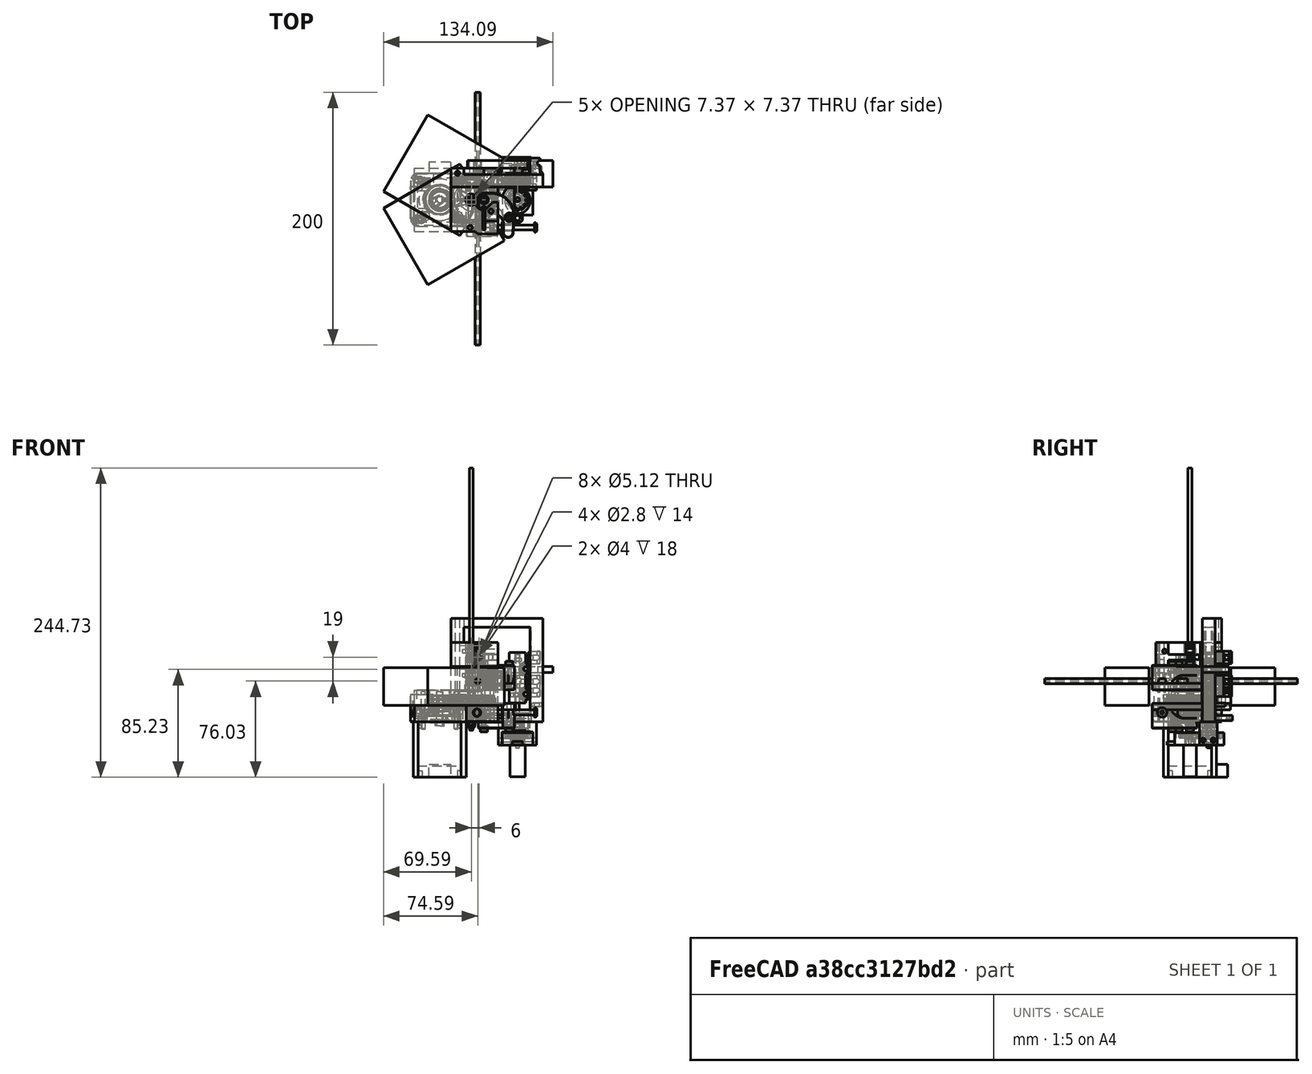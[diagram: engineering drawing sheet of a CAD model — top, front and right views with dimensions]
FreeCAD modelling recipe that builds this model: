
FCSTD DOCUMENT  (FreeCAD 0.17R13541 (Git))
Label: multi-drive
License: All rights reserved
LicenseURL: http://en.wikipedia.org/wiki/All_rights_reserved
objects: Part::Cylinder×120, Part::Feature×74, Part::MultiFuse×72, Part::Box×64, Part::Cut×51, Part::Mirroring×21, Part::Chamfer×13, App::DocumentObjectGroup×8, Part::Fillet×5, Part::MultiCommon×2, Part::Fuse×2
note: 424 computed .brp shape members not serialized (recipe doc carries the construction recipe); baked Part::Feature solids carry a one-line shape summary decoded from their .brp

FEATURE [Part::Feature] Part__Feature  label="408"
  Placement = pos=(-0.0297872,0.0238949,-17.7265) rot=(0,0,-1;1.5708rad)
  shape: bbox 42 x 50.7 x 67.75 mm, 52 faces (baked)
FEATURE [Part::Feature] Part__Feature001  label="279"
  Placement = pos=(33.9857,-1.05205,32.8235) rot=(0.910043,0.414513,0;3.14159rad)
  shape: bbox 10 x 10 x 4 mm, 22 faces (baked)
FEATURE [Part::Feature] Part__Feature002  label="1308_lasercut"
  Placement = pos=(34.9702,0.079623,40.5235) rot=(1,0,0;3.14159rad)
  shape: bbox 28.5 x 62 x 5 mm, 26 faces (baked)
FEATURE [Part::Feature] Part__Feature003  label="1309"
  Placement = pos=(34.9702,0.079623,29.0235) rot=(1,0,0;3.14159rad)
  shape: bbox 39.69 x 36.58 x 16.55 mm, 81 faces (baked)
FEATURE [Part::Feature] Part__Feature004  label="1193"
  Placement = pos=(39.781,-21.9761,33.5235) rot=(0.447214,0.774597,0.447214;1.82348rad)
  shape: bbox 3.2 x 7 x 8.083 mm, 26 faces (baked)
FEATURE [Part::Feature] Part__Feature005  label="650"
  Placement = pos=(74.781,-21.9761,33.5235) rot=(-0.322847,0.889685,-0.322847;1.68742rad)
  shape: bbox 37.2 x 8.193 x 8.193 mm, 18 faces (baked)
FEATURE [Part::Feature] Part__Feature006  label="1185"
  Placement = pos=(49.1702,-21.9761,33.5235) rot=(0.682107,-0.263555,0.682107;3.65698rad)
  shape: bbox 0.8 x 9 x 9 mm, 6 faces (baked)
FEATURE [Part::Feature] Part__Feature007  label="212"
  Placement = pos=(34.9702,0.079623,35.8235) rot=(0.929679,0.36837,0;3.14159rad)
  shape: bbox 7 x 7 x 0.5 mm, 6 faces (baked)
FEATURE [Part::Feature] Part__Feature008  label="257"
  Placement = pos=(34.9702,0.079623,21.0235) rot=(0.969952,-0.243295,0;3.14159rad)
  shape: bbox 5.7 x 5.7 x 15 mm, 16 faces (baked)
FEATURE [Part::Feature] Part__Feature009  label="1183"
  Placement = pos=(5.97021,0.0238949,29.13) rot=(0,0.831219,-0.555945;3.14159rad)
  shape: bbox 4 x 3 x 3 mm, 15 faces (baked)
FEATURE [Part::Feature] Part__Feature010  label="212001"
  Placement = pos=(24.9702,0.0238949,26.1235) rot=(0.905883,0.423527,0;3.14159rad)
  shape: bbox 7 x 7 x 0.5 mm, 6 faces (baked)
FEATURE [Part::Feature] Part__Feature011  label="212002"
  Placement = pos=(34.9702,0.079623,31.3235) rot=(0.929679,0.36837,0;3.14159rad)
  shape: bbox 7 x 7 x 0.5 mm, 6 faces (baked)
FEATURE [Part::Feature] Part__Feature012  label="448"
  Placement = pos=(24.9702,0.0238949,30.1235) rot=(0,0,1;0rad)
  shape: bbox 8.761 x 8.744 x 6.4 mm, 204 faces (baked)
FEATURE [Part::Feature] Part__Feature013  label="423"
  Placement = pos=(24.9702,0.0238949,39.0235) rot=(0,0,1;0.10732rad)
  shape: bbox 9 x 9 x 4 mm, 22 faces (baked)
FEATURE [Part::Feature] Part__Feature014  label="423001"
  Placement = pos=(24.9702,0.0238949,28.6235) rot=(0,0,1;3.74342rad)
  shape: bbox 9 x 9 x 4 mm, 22 faces (baked)
FEATURE [Part::Feature] Part__Feature015  label="113"
  Placement = pos=(24.9702,0.0238949,44.4235) rot=(0,0,1;3.01463rad)
  shape: bbox 6.3 x 5.858 x 27.5 mm, 19 faces (baked)
FEATURE [Part::Feature] Part__Feature016  label="204"
  Placement = pos=(24.9702,0.0238949,25.6235) rot=(0.995731,-0.092303,0;3.14159rad)
  shape: bbox 6.243 x 5.99 x 4 mm, 28 faces (baked)
FEATURE [Part::Feature] Part__Feature017  label="1310_ISO - RH Helical gear 1M 17T 45HA 20PA 12FW ---17A75H50L0.8N"
  Placement = pos=(-0.0297872,0.0238949,43.5235) rot=(0.464719,0.753705,-0.464719;1.84986rad)
  shape: bbox 18 x 18 x 13.32 mm, 178 faces (baked)
FEATURE [Part::Feature] Part__Feature018  label="1311_ISO - RH Helical gear 1M 17T 45HA 20PA 12FW ---17A75H50L0.8N"
  Placement = pos=(24.9702,0.0238949,47.0235) rot=(0.063312,0.995983,-0.063312;1.57482rad)
  shape: bbox 37.39 x 37.38 x 6 mm, 421 faces (baked)
FEATURE [Part::Feature] Part__Feature019  label="1306"
  Placement = pos=(-0.0297872,0.0238949,26.0235) rot=(0,0,-1;1.5708rad)
  shape: bbox 70.89 x 54.16 x 21.5 mm, 245 faces (baked)
FEATURE [Part::Feature] Part__Feature020  label="257001"
  Placement = pos=(34.9702,-8.92038,21.0235) rot=(0.016076,0.999871,0;3.14159rad)
  shape: bbox 5.7 x 5.7 x 15 mm, 16 faces (baked)
FEATURE [Part::Feature] Part__Feature021  label="257002"
  Placement = pos=(54.9702,-13.9204,21.0235) rot=(0.293708,0.955895,0;3.14159rad)
  shape: bbox 5.7 x 5.7 x 15 mm, 16 faces (baked)
FEATURE [Part::Feature] Part__Feature022  label="257003"
  Placement = pos=(-15.5298,15.5239,35.5235) rot=(0,0,1;0.425248rad)
  shape: bbox 5.7 x 5.7 x 15 mm, 16 faces (baked)
FEATURE [Part::Feature] Part__Feature023  label="257004"
  Placement = pos=(15.4702,-15.4761,35.5235) rot=(0,0,1;0.425248rad)
  shape: bbox 5.7 x 5.7 x 15 mm, 16 faces (baked)
FEATURE [Part::Feature] Part__Feature024  label="257005"
  Placement = pos=(15.4702,15.5239,35.5235) rot=(0,0,1;0.425248rad)
  shape: bbox 5.7 x 5.7 x 15 mm, 16 faces (baked)
FEATURE [Part::Feature] Part__Feature025  label="257006"
  Placement = pos=(-15.5298,-15.4761,35.5235) rot=(0,0,1;1.70042rad)
  shape: bbox 5.7 x 5.7 x 15 mm, 16 faces (baked)
FEATURE [Part::Feature] Part__Feature026  label="212003"
  Placement = pos=(24.9702,0.0238949,41.0235) rot=(0.929679,0.36837,0;3.14159rad)
  shape: bbox 7 x 7 x 0.5 mm, 6 faces (baked)
FEATURE [App::DocumentObjectGroup] Group  label="original-geared-extruder"
  Group = -> [Part__Feature,Part__Feature001,Part__Feature002,Part__Feature003,Part__Feature004,Part__Feature005,Part__Feature006,Part__Feature007,Part__Feature008,Part__Feature009,Part__Feature010,Part__Feature011,Part__Feature012,Part__Feature013,Part__Feature014,Part__Feature015,Part__Feature016,Part__Feature017,Part__Feature018,Part__Feature019,Part__Feature020,Part__Feature021,Part__Feature022,+4 more]
FEATURE [Part::Box] Box  label="Cube"
  AttacherType = Attacher::AttachEngine3D
  Height = 35
  Length = 35
  Placement = pos=(-17.5,-17.5,-9) rot=(0,0,1;0rad)
  Width = 35
FEATURE [Part::Cylinder] Cylinder
  Angle = 360
  AttacherType = Attacher::AttachEngine3D
  Height = 25
  Placement = pos=(0,0,25) rot=(0,0,1;0rad)
  Radius = 2.5
FEATURE [Part::Cylinder] Cylinder001
  Angle = 360
  AttacherType = Attacher::AttachEngine3D
  Height = 2
  Placement = pos=(0,0,25) rot=(0,0,1;0rad)
  Radius = 11
FEATURE [Part::Cylinder] Cylinder002
  Angle = 360
  AttacherType = Attacher::AttachEngine3D
  Height = 25
  Placement = pos=(13,13,25) rot=(0,0,1;0rad)
  Radius = 1.5
FEATURE [Part::Cylinder] Cylinder003
  Angle = 360
  AttacherType = Attacher::AttachEngine3D
  Height = 25
  Placement = pos=(-13,13,25) rot=(0,0,1;0rad)
  Radius = 1.5
FEATURE [Part::Cylinder] Cylinder004
  Angle = 360
  AttacherType = Attacher::AttachEngine3D
  Height = 25
  Placement = pos=(13,-13,25) rot=(0,0,1;0rad)
  Radius = 1.5
FEATURE [Part::Cylinder] Cylinder005
  Angle = 360
  AttacherType = Attacher::AttachEngine3D
  Height = 25
  Placement = pos=(-13,-13,25) rot=(0,0,1;0rad)
  Radius = 1.5
FEATURE [Part::Feature] Part__Feature027  label="1310"
  Placement = pos=(0,0,40.5235) rot=(0.464719,0.753705,-0.464719;1.84986rad)
  shape: bbox 18 x 18 x 13.32 mm, 178 faces (baked)
FEATURE [Part::Feature] Part__Feature028  label="1311"
  Placement = pos=(24.9702,0.0238949,47.0235) rot=(0.063312,0.995983,-0.063312;1.57482rad)
  shape: bbox 37.39 x 37.38 x 6 mm, 421 faces (baked)
FEATURE [Part::Feature] Part__Feature029  label="257003001"
  Placement = pos=(-13,13,32.5) rot=(0,0,1;0.425248rad)
  shape: bbox 5.7 x 5.7 x 15 mm, 16 faces (baked)
FEATURE [Part::Feature] Part__Feature030  label="257003002"
  Placement = pos=(13,13,32.5) rot=(0,0,1;0.425248rad)
  shape: bbox 5.7 x 5.7 x 15 mm, 16 faces (baked)
FEATURE [Part::Feature] Part__Feature031  label="257003003"
  Placement = pos=(13,-13,32.5) rot=(0,0,1;0.425248rad)
  shape: bbox 5.7 x 5.7 x 15 mm, 16 faces (baked)
FEATURE [Part::Feature] Part__Feature032  label="257003004"
  Placement = pos=(-13,-13,32.5) rot=(0,0,1;0.425248rad)
  shape: bbox 5.7 x 5.7 x 15 mm, 16 faces (baked)
FEATURE [App::DocumentObjectGroup] Group001  label="NEMA-14"
  Group = -> [Box,Cylinder,Cylinder001,Cylinder002,Cylinder003,Cylinder004,Cylinder005,Part__Feature029,Part__Feature030,Part__Feature031,Part__Feature032]
FEATURE [Part::Cylinder] Cylinder006  label="big-gear-centre"
  Angle = 360
  AttacherType = Attacher::AttachEngine3D
  Height = 6
  Placement = pos=(25,0,41) rot=(0,0,1;0rad)
  Radius = 14
FEATURE [Part::MultiFuse] Fusion  label="1311-a"
  Placement = pos=(0,0,-3) rot=(0,0,1;0rad)
  Shapes = -> [Part__Feature028,Cylinder006]
FEATURE [Part::Cylinder] Cylinder007  label="m3-studding"
  Angle = 360
  AttacherType = Attacher::AttachEngine3D
  Height = 200
  Placement = pos=(25,0,27) rot=(0,0,1;0rad)
  Radius = 1.5
FEATURE [Part::Box] Box001  label="Cube001"
  AttacherType = Attacher::AttachEngine3D
  Height = 25
  Length = 66
  Placement = pos=(-20,-25,26) rot=(0,0,1;0rad)
  Width = 50
FEATURE [Part::Cylinder] Cylinder008
  Angle = 360
  AttacherType = Attacher::AttachEngine3D
  Height = 25
  Placement = pos=(13,13,25) rot=(0,0,1;0rad)
  Radius = 1.7
FEATURE [Part::Cylinder] Cylinder012
  Angle = 360
  AttacherType = Attacher::AttachEngine3D
  Height = 25
  Placement = pos=(13,13,35.5) rot=(0,0,1;0rad)
  Radius = 3.5
FEATURE [Part::Cylinder] Cylinder016  label="big-gear-hole"
  Angle = 360
  AttacherType = Attacher::AttachEngine3D
  Height = 20
  Placement = pos=(25,0,37.5) rot=(0,0,1;0rad)
  Radius = 19.5
FEATURE [Part::Cylinder] Cylinder017  label="small-gear-hole"
  Angle = 360
  AttacherType = Attacher::AttachEngine3D
  Height = 33
  Placement = pos=(0,0,25) rot=(0,0,1;0rad)
  Radius = 12
FEATURE [Part::Cylinder] Cylinder018  label="hole-for-shaft"
  Angle = 360
  AttacherType = Attacher::AttachEngine3D
  Height = 30
  Placement = pos=(25,0,24) rot=(0,0,1;0rad)
  Radius = 3.6
FEATURE [Part::Cylinder] Cylinder019  label="9mm-bearing"
  Angle = 360
  AttacherType = Attacher::AttachEngine3D
  Height = 30
  Placement = pos=(25,0,32.5) rot=(0,0,1;0rad)
  Radius = 4.5
FEATURE [Part::Cylinder] Cylinder020
  Angle = 360
  AttacherType = Attacher::AttachEngine3D
  Height = 25
  Placement = pos=(16,13,25) rot=(0,0,1;0rad)
  Radius = 1.7
FEATURE [Part::Cylinder] Cylinder021
  Angle = 360
  AttacherType = Attacher::AttachEngine3D
  Height = 25
  Placement = pos=(16,13,35.5) rot=(0,0,1;0rad)
  Radius = 3.5
FEATURE [Part::Box] Box002  label="Cube002"
  AttacherType = Attacher::AttachEngine3D
  Height = 15
  Length = 3
  Placement = pos=(13,11.3,25) rot=(0,0,1;0rad)
  Width = 3.4
FEATURE [Part::Box] Box003  label="Cube003"
  AttacherType = Attacher::AttachEngine3D
  Height = 25
  Length = 3
  Placement = pos=(13,9.5,35.5) rot=(0,0,1;0rad)
  Width = 7
FEATURE [Part::MultiFuse] Fusion001  label="M3-slot"
  Placement = pos=(-1.5,0,0) rot=(0,0,1;0rad)
  Shapes = -> [Cylinder008,Box003,Cylinder020,Cylinder012,Box002,Cylinder021]
FEATURE [Part::MultiFuse] Fusion002  label="M3-slot001"
  Placement = pos=(-27.5,0,0) rot=(0,0,1;0rad)
  Shapes = -> [Cylinder008,Box003,Cylinder020,Cylinder012,Box002,Cylinder021]
FEATURE [Part::MultiFuse] Fusion003  label="M3-slot002"
  Placement = pos=(-27.5,-26,0) rot=(0,0,1;0rad)
  Shapes = -> [Cylinder008,Box003,Cylinder020,Cylinder012,Box002,Cylinder021]
FEATURE [Part::MultiFuse] Fusion004  label="M3-slot003"
  Placement = pos=(-1.5,-26,0) rot=(0,0,1;0rad)
  Shapes = -> [Cylinder008,Box003,Cylinder020,Cylinder012,Box002,Cylinder021]
FEATURE [Part::MultiFuse] Fusion005  label="M3-slots"
  Placement = pos=(0,0,-3) rot=(0,0,1;0rad)
  Shapes = -> [Fusion001,Fusion002,Fusion003,Fusion004]
FEATURE [Part::MultiFuse] Fusion006  label="gear-holes"
  Shapes = -> [Cylinder017,Cylinder016]
FEATURE [Part::MultiFuse] Fusion007  label="bearing-and-shaft-holes"
  Shapes = -> [Cylinder018,Cylinder019]
FEATURE [Part::MultiFuse] Fusion008
  Shapes = -> [Fusion005,Fusion007,Fusion006]
FEATURE [Part::Cut] Cut  label="blank-gearbox-a"
  Base = -> Box001
  Tool = -> Fusion008
FEATURE [Part::Feature] Part__Feature034  label="204001"
  Placement = pos=(24.9702,0.0238949,25.6235) rot=(0.995731,-0.092303,0;3.14159rad)
  shape: bbox 6.243 x 5.99 x 4 mm, 28 faces (baked)
FEATURE [Part::Feature] Part__Feature035  label="423001001"
  Placement = pos=(24.9702,0.0238949,53.5235) rot=(0,0,1;3.74342rad)
  shape: bbox 9 x 9 x 4 mm, 22 faces (baked)
FEATURE [Part::Feature] Part__Feature036  label="423001002"
  Placement = pos=(24.9702,0.0238949,63.9235) rot=(0,0,1;0.10732rad)
  shape: bbox 9 x 9 x 4 mm, 22 faces (baked)
FEATURE [Part::Feature] Part__Feature037  label="448001"
  Placement = pos=(24.9702,0.0238949,55.0235) rot=(0,0,1;0rad)
  shape: bbox 8.761 x 8.744 x 6.4 mm, 204 faces (baked)
FEATURE [Part::Feature] Part__Feature038  label="212001001"
  Placement = pos=(24.9702,0.0238949,26.1235) rot=(0.905883,0.423527,0;3.14159rad)
  shape: bbox 7 x 7 x 0.5 mm, 6 faces (baked)
FEATURE [Part::Mirroring] Part__Mirroring  label="204001 (Mirror #1)"
  Base = (0,0,0)
  Normal = (0,0,1)
  Placement = pos=(0,0,91.6) rot=(0,0,1;0rad)
  Source = -> Part__Feature034
FEATURE [Part::Mirroring] Part__Mirroring001  label="212001001 (Mirror #2)"
  Base = (0,0,0)
  Normal = (0,0,1)
  Placement = pos=(0,0,91.6) rot=(0,0,1;0rad)
  Source = -> Part__Feature038
FEATURE [Part::Feature] Part__Feature040  label="204001001"
  Placement = pos=(24.9702,0.0238949,51.6235) rot=(0.995731,-0.092303,0;3.14159rad)
  shape: bbox 6.243 x 5.99 x 4 mm, 28 faces (baked)
FEATURE [Part::Mirroring] Part__Mirroring002  label="204001001 (Mirror #3)"
  Base = (0,0,0)
  Normal = (0,0,1)
  Placement = pos=(0,0,98.7) rot=(0,0,1;0rad)
  Source = -> Part__Feature040
FEATURE [Part::MultiFuse] Fusion009  label="hob-assembly"
  Shapes = -> [Part__Mirroring001,Part__Feature037,Part__Feature035,Part__Feature036,Part__Mirroring]
FEATURE [Part::MultiFuse] Fusion010  label="hob-assembly001"
  Placement = pos=(0,0,19) rot=(0,0,1;0rad)
  Shapes = -> [Part__Mirroring001,Part__Feature037,Part__Feature035,Part__Feature036,Part__Mirroring]
FEATURE [Part::Feature] Part__Feature041  label="279001"
  Placement = pos=(33.9857,-1.05205,57.8235) rot=(0.910043,0.414513,0;3.14159rad)
  shape: bbox 10 x 10 x 4 mm, 22 faces (baked)
FEATURE [Part::Feature] Part__Feature042  label="1308_lasercut001"
  Placement = pos=(34.9702,0.079623,65.5235) rot=(1,0,0;3.14159rad)
  shape: bbox 28.5 x 62 x 5 mm, 26 faces (baked)
FEATURE [Part::Feature] Part__Feature043  label="1309001"
  Placement = pos=(34.9702,0.079623,54.0235) rot=(1,0,0;3.14159rad)
  shape: bbox 39.69 x 36.58 x 16.55 mm, 81 faces (baked)
FEATURE [Part::Feature] Part__Feature044  label="212001002"
  Placement = pos=(34.9702,0.079623,60.8235) rot=(0.929679,0.36837,0;3.14159rad)
  shape: bbox 7 x 7 x 0.5 mm, 6 faces (baked)
FEATURE [Part::Feature] Part__Feature045  label="257003005"
  Placement = pos=(34.9702,0.079623,46.0235) rot=(0.969952,-0.243295,0;3.14159rad)
  shape: bbox 5.7 x 5.7 x 15 mm, 16 faces (baked)
FEATURE [Part::Feature] Part__Feature046  label="212002001"
  Placement = pos=(34.9702,0.079623,56.3235) rot=(0.929679,0.36837,0;3.14159rad)
  shape: bbox 7 x 7 x 0.5 mm, 6 faces (baked)
FEATURE [Part::Feature] Part__Feature047  label="257001001"
  Placement = pos=(34.9702,-8.92038,46.0235) rot=(0.016076,0.999871,0;3.14159rad)
  shape: bbox 5.7 x 5.7 x 15 mm, 16 faces (baked)
FEATURE [Part::Feature] Part__Feature048  label="257002001"
  Placement = pos=(54.9702,-13.9204,46.0235) rot=(0.293708,0.955895,0;3.14159rad)
  shape: bbox 5.7 x 5.7 x 15 mm, 16 faces (baked)
FEATURE [Part::Mirroring] Part__Mirroring003  label="279001 (Mirror #4)"
  Base = (0,0,0)
  Normal = (0,0,1)
  Placement = pos=(1,0,116.5) rot=(0,0,1;0rad)
  Source = -> Part__Feature041
FEATURE [Part::Mirroring] Part__Mirroring004  label="1308_lasercut001 (Mirror #5)"
  Base = (0,0,0)
  Normal = (0,0,1)
  Placement = pos=(0,0,117) rot=(0,0,1;0rad)
  Source = -> Part__Feature042
FEATURE [Part::Mirroring] Part__Mirroring005  label="1309001 (Mirror #6)"
  Base = (0,0,0)
  Normal = (0,0,1)
  Placement = pos=(0,0,117) rot=(0,0,1;0rad)
  Source = -> Part__Feature043
FEATURE [Part::Mirroring] Part__Mirroring006  label="212001002 (Mirror #7)"
  Base = (0,0,0)
  Normal = (0,0,1)
  Placement = pos=(1,0,116.5) rot=(0,0,1;0rad)
  Source = -> Part__Feature044
FEATURE [Part::Mirroring] Part__Mirroring007  label="257003005 (Mirror #8)"
  Base = (0,0,0)
  Normal = (0,0,1)
  Placement = pos=(0,0,117) rot=(0,0,1;0rad)
  Source = -> Part__Feature045
FEATURE [Part::Mirroring] Part__Mirroring008  label="212002001 (Mirror #9)"
  Base = (0,0,0)
  Normal = (0,0,1)
  Placement = pos=(1,0,116.5) rot=(0,0,1;0rad)
  Source = -> Part__Feature046
FEATURE [Part::Mirroring] Part__Mirroring009  label="257001001 (Mirror #10)"
  Base = (0,0,0)
  Normal = (0,0,1)
  Placement = pos=(0,0,117) rot=(0,0,1;0rad)
  Source = -> Part__Feature047
FEATURE [Part::Mirroring] Part__Mirroring010  label="257002001 (Mirror #11)"
  Base = (0,0,0)
  Normal = (0,0,1)
  Placement = pos=(0,0,117) rot=(0,0,1;0rad)
  Source = -> Part__Feature048
FEATURE [Part::Cylinder] Cylinder022  label="filament"
  Angle = 360
  AttacherType = Attacher::AttachEngine3D
  Height = 200
  Placement = pos=(30,85,58.3) rot=(1,0,0;1.5708rad)
  Radius = 0.875
FEATURE [Part::Box] Box004  label="Cube004"
  AttacherType = Attacher::AttachEngine3D
  Height = 19
  Length = 32
  Placement = pos=(14,-25,51) rot=(0,0,1;0rad)
  Width = 50
FEATURE [Part::Box] Box005  label="Cube005"
  AttacherType = Attacher::AttachEngine3D
  Height = 4
  Length = 14
  Placement = pos=(20.0359,-19.6506,51.6) rot=(0,0,-1;0.523599rad)
  Width = 44
FEATURE [Part::Box] Box006  label="Cube006"
  AttacherType = Attacher::AttachEngine3D
  Height = 4
  Length = 14
  Placement = pos=(20.0359,-19.6506,60.7) rot=(0,0,-1;0.523599rad)
  Width = 44
FEATURE [Part::Feature] Part__Feature049  label="257006001"
  Placement = pos=(36,0,64) rot=(0,0,1;1.70042rad)
  shape: bbox 5.7 x 5.7 x 15 mm, 16 faces (baked)
FEATURE [Part::Feature] Part__Feature050  label="257006001001"
  Placement = pos=(41.5,-9,64) rot=(0,0,1;2.22402rad)
  shape: bbox 5.7 x 5.7 x 15 mm, 16 faces (baked)
FEATURE [Part::Box] Box008  label="Cube008"
  AttacherType = Attacher::AttachEngine3D
  Height = 6
  Length = 10
  Placement = pos=(36,3,54.7) rot=(0,0,1;0rad)
  Width = 22
FEATURE [Part::Feature] Part__Feature051  label="257006001001001"
  Placement = pos=(42,22,64) rot=(0,0,1;1.70042rad)
  shape: bbox 5.7 x 5.7 x 15 mm, 16 faces (baked)
FEATURE [Part::Feature] Part__Feature052  label="257006001001002"
  Placement = pos=(42.5,7,64) rot=(0,0,1;1.70042rad)
  shape: bbox 5.7 x 5.7 x 15 mm, 16 faces (baked)
FEATURE [Part::Box] Box009  label="Cube009"
  AttacherType = Attacher::AttachEngine3D
  Height = 4
  Length = 10
  Placement = pos=(36,-15,51.6) rot=(0,0,1;0rad)
  Width = 40
FEATURE [Part::Box] Box010  label="Cube010"
  AttacherType = Attacher::AttachEngine3D
  Height = 4
  Length = 10
  Placement = pos=(36,-15,60.7) rot=(0,0,1;0rad)
  Width = 40
FEATURE [Part::Box] Box012  label="Cube012"
  AttacherType = Attacher::AttachEngine3D
  Height = 30
  Length = 70
  Placement = pos=(-9.5859,-67.3109,39) rot=(0,0,1;0.523599rad)
  Width = 70
FEATURE [Part::Box] Box013  label="Cube013"
  AttacherType = Attacher::AttachEngine3D
  Height = 30
  Length = 70
  Placement = pos=(-44.5859,6.68911,39) rot=(0,0,-1;0.523599rad)
  Width = 70
FEATURE [Part::Box] Box014  label="Cube014"
  AttacherType = Attacher::AttachEngine3D
  Height = 30
  Length = 70
  Placement = pos=(-9.5859,-67.3109,39) rot=(0,0,1;0.523599rad)
  Width = 70
FEATURE [Part::Cylinder] Cylinder024  label="Cylinder022"
  Angle = 360
  AttacherType = Attacher::AttachEngine3D
  Height = 4
  Placement = pos=(38,0,60.7) rot=(0,0,1;0rad)
  Radius = 6
FEATURE [Part::Cylinder] Cylinder025  label="Cylinder023"
  Angle = 360
  AttacherType = Attacher::AttachEngine3D
  Height = 4
  Placement = pos=(38,0,51.6) rot=(0,0,1;0rad)
  Radius = 6
FEATURE [Part::Chamfer] Chamfer001
  Base = -> Box008
  Edges = 1 edges r=5.5: [Edge1]
FEATURE [Part::Cylinder] Cylinder026  label="pneumatic-clearance"
  Angle = 360
  AttacherType = Attacher::AttachEngine3D
  Height = 200
  Placement = pos=(30,85,58.3) rot=(1,0,0;1.5708rad)
  Radius = 2
FEATURE [Part::Cylinder] Cylinder028  label="bearing-through-hole001"
  Angle = 360
  AttacherType = Attacher::AttachEngine3D
  Height = 200
  Placement = pos=(25,0,38) rot=(0,0,1;0rad)
  Radius = 4.5
FEATURE [Part::Box] Box017  label="Cube017"
  AttacherType = Attacher::AttachEngine3D
  Height = 19
  Length = 26
  Placement = pos=(9,-25,51) rot=(0,0,1;0rad)
  Width = 50
FEATURE [Part::Cut] Cut003
  Base = -> Box017
  Tool = -> Cylinder028
FEATURE [Part::Cylinder] Cylinder029  label="Cylinder025"
  Angle = 360
  AttacherType = Attacher::AttachEngine3D
  Height = 40
  Placement = pos=(36,0,41) rot=(0,0,1;0rad)
  Radius = 8.5
FEATURE [Part::Cut] Cut004
  Base = -> Cut003
  Tool = -> Cylinder029
FEATURE [Part::Cylinder] Cylinder031  label="m3-studding002"
  Angle = 360
  AttacherType = Attacher::AttachEngine3D
  Height = 200
  Placement = pos=(14,21,0) rot=(0,0,1;0rad)
  Radius = 1.75
FEATURE [Part::Cylinder] Cylinder032  label="m3-studding003"
  Angle = 360
  AttacherType = Attacher::AttachEngine3D
  Height = 200
  Placement = pos=(24,-22,0) rot=(0,0,1;0rad)
  Radius = 1.75
FEATURE [Part::Box] Box018  label="Cube018"
  AttacherType = Attacher::AttachEngine3D
  Height = 25
  Length = 66
  Placement = pos=(-31.8236,-10.815,45) rot=(0,0,-1;0.122173rad)
  Width = 50
FEATURE [Part::Box] Box019  label="Cube019"
  AttacherType = Attacher::AttachEngine3D
  Height = 25
  Length = 66
  Placement = pos=(-31.8236,-10.815,45) rot=(0,0,-1;0.122173rad)
  Width = 50
FEATURE [Part::MultiFuse] Fusion012
  Shapes = -> [Box009,Chamfer001]
FEATURE [Part::Cut] Cut007
  Base = -> Fusion012
  Tool = -> Box018
FEATURE [Part::Cut] Cut008
  Base = -> Box010
  Tool = -> Box019
FEATURE [Part::MultiFuse] Fusion013
  Shapes = -> [Cylinder024,Cut008]
FEATURE [Part::MultiFuse] Fusion014
  Shapes = -> [Cylinder025,Cut007]
FEATURE [Part::Cylinder] Cylinder033  label="1250"
  Angle = 360
  AttacherType = Attacher::AttachEngine3D
  Height = 8
  Placement = pos=(41,15,58) rot=(0,1,0;1.5708rad)
  Radius = 3.25
FEATURE [Part::Cylinder] Cylinder034  label="wing-clearance"
  Angle = 360
  AttacherType = Attacher::AttachEngine3D
  Height = 9
  Placement = pos=(25,0,41) rot=(0,0,1;0rad)
  Radius = 9
FEATURE [Part::Feature] Part__Feature055  label="M6 thread"
  Placement = pos=(30,25,58.3) rot=(0.935113,0.250563,-0.250563;1.63783rad)
  shape: bbox 10 x 5.798 x 11.55 mm, 23 faces (baked)
FEATURE [Part::Cylinder] Cylinder035  label="filament001"
  Angle = 360
  AttacherType = Attacher::AttachEngine3D
  Height = 50
  Placement = pos=(30,47,58.3) rot=(1,0,0;1.5708rad)
  Radius = 2
FEATURE [Part::Cylinder] Cylinder036  label="filament002"
  Angle = 360
  AttacherType = Attacher::AttachEngine3D
  Height = 6
  Placement = pos=(30,25.5,58.3) rot=(1,0,0;1.5708rad)
  Radius = 4.5
FEATURE [Part::MultiFuse] Fusion017  label="driven-side-ptfe"
  Shapes = -> [Cylinder035,Cylinder036]
FEATURE [Part::Cylinder] Cylinder037  label="filament003"
  Angle = 360
  AttacherType = Attacher::AttachEngine3D
  Height = 50
  Placement = pos=(30,-1,58.3) rot=(1,0,0;1.5708rad)
  Radius = 1.5
FEATURE [Part::Cylinder] Cylinder038  label="filament004"
  Angle = 360
  AttacherType = Attacher::AttachEngine3D
  Height = 50
  Placement = pos=(30,-9,58.3) rot=(1,0,0;1.5708rad)
  Radius = 2
FEATURE [Part::MultiFuse] Fusion019  label="draw-side-ptfe"
  Shapes = -> [Cylinder037,Cylinder038]
FEATURE [Part::Cylinder] Cylinder039  label="filament005"
  Angle = 360
  AttacherType = Attacher::AttachEngine3D
  Height = 10
  Placement = pos=(30,21,58.3) rot=(1,0,0;1.5708rad)
  Radius = 22
FEATURE [Part::Box] Box020  label="Cube020"
  AttacherType = Attacher::AttachEngine3D
  Height = 53
  Length = 110
  Placement = pos=(-61,8,30.5) rot=(0,0,1;0rad)
  Width = 15
FEATURE [Part::Box] Box022  label="Cube022"
  AttacherType = Attacher::AttachEngine3D
  Height = 10
  Length = 8
  Placement = pos=(41,12.5,58) rot=(0,0,1;0rad)
  Width = 7
FEATURE [Part::Cylinder] Cylinder040  label="1250001"
  Angle = 360
  AttacherType = Attacher::AttachEngine3D
  Height = 8
  Placement = pos=(41,16,58) rot=(0,1,0;1.5708rad)
  Radius = 3.5
FEATURE [Part::MultiFuse] Fusion020  label="spring-cavity"
  Placement = pos=(0,-1,0) rot=(0,0,1;0rad)
  Shapes = -> [Box022,Cylinder040]
FEATURE [Part::Cut] Cut013
  Base = -> Fusion014
  Tool = -> Fusion020
FEATURE [Part::Cylinder] Cylinder041  label="1250002"
  Angle = 360
  AttacherType = Attacher::AttachEngine3D
  Height = 8
  Placement = pos=(41,16,58) rot=(0,1,0;1.5708rad)
  Radius = 3.5
FEATURE [Part::Box] Box023  label="Cube023"
  AttacherType = Attacher::AttachEngine3D
  Height = 6
  Length = 3
  Placement = pos=(43,-1.2,54.7) rot=(0,0,1;0rad)
  Width = 6
FEATURE [Part::MultiFuse] Fusion021
  Shapes = -> [Cut013,Box023]
FEATURE [Part::Box] Box024  label="Cube024"
  AttacherType = Attacher::AttachEngine3D
  Height = 9.1
  Length = 1
  Placement = pos=(44.784,-0.65857,51.6) rot=(0,0,-1;0.383972rad)
  Width = 13.5
FEATURE [Part::Box] Box025  label="Cube025"
  AttacherType = Attacher::AttachEngine3D
  Height = 53
  Length = 110
  Placement = pos=(-45,8,64.7) rot=(0,0,1;0rad)
  Width = 15
FEATURE [Part::Box] Box026  label="Cube026"
  AttacherType = Attacher::AttachEngine3D
  Height = 53
  Length = 110
  Placement = pos=(-42,8,-1.4) rot=(0,0,1;0rad)
  Width = 15
FEATURE [Part::MultiFuse] Fusion023  label="bump-chop001"
  Shapes = -> [Box020,Box025,Box026]
FEATURE [Part::Cylinder] Cylinder042  label="filament006"
  Angle = 360
  AttacherType = Attacher::AttachEngine3D
  Height = 2.8
  Placement = pos=(30,21,58.3) rot=(1,0,0;1.5708rad)
  Radius = 23
FEATURE [Part::Cylinder] Cylinder043  label="filament007"
  Angle = 360
  AttacherType = Attacher::AttachEngine3D
  Height = 2.8
  Placement = pos=(30,13.8,58.3) rot=(1,0,0;1.5708rad)
  Radius = 23
FEATURE [Part::MultiFuse] Fusion024
  Shapes = -> [Cylinder042,Cylinder043,Cylinder039]
FEATURE [Part::Cut] Cut015
  Base = -> Fusion024
  Tool = -> Fusion023
FEATURE [Part::Chamfer] Chamfer004
  Base = -> Cut015
  Edges = 4 edges r=0.95: [Edge4,Edge5,Edge33,Edge35]
  Placement = pos=(0,-1,0) rot=(0,0,1;0rad)
FEATURE [Part::Fillet] Fillet
  Base = -> Chamfer004
  Edges = 2 edges r=1.5: [Edge17,Edge27]
FEATURE [Part::MultiFuse] Fusion025  label="wedge-clamp-a"
  Shapes = -> [Fusion021,Box024,Fillet]
FEATURE [Part::Box] Box027  label="Cube027"
  AttacherType = Attacher::AttachEngine3D
  Height = 10
  Length = 2
  Placement = pos=(41,11.5,58) rot=(0,0,1;0rad)
  Width = 7
FEATURE [Part::Cylinder] Cylinder044  label="1250003"
  Angle = 360
  AttacherType = Attacher::AttachEngine3D
  Height = 8
  Placement = pos=(41,15,58) rot=(0,1,0;1.5708rad)
  Radius = 3.5
FEATURE [Part::MultiFuse] Fusion026  label="sprint-adj-hole"
  Shapes = -> [Box027,Cylinder044]
FEATURE [Part::Cut] Cut016  label="clamp-plate-a"
  Base = -> Fusion013
  Tool = -> Fusion026
FEATURE [Part::Feature] Part__Feature056  label="423001003"
  Placement = pos=(55,14.5,58) rot=(1,0,0;1.5708rad)
  shape: bbox 9 x 4 x 9 mm, 22 faces (baked)
FEATURE [Part::Feature] Part__Feature057  label="423001003001"
  Placement = pos=(68,14.5,48) rot=(1,0,0;1.5708rad)
  shape: bbox 9 x 4 x 9 mm, 22 faces (baked)
FEATURE [Part::Cylinder] Cylinder045  label="m3-studding004"
  Angle = 360
  AttacherType = Attacher::AttachEngine3D
  Height = 200
  Placement = pos=(61.5,15,2) rot=(0,0,1;0rad)
  Radius = 1.9
FEATURE [Part::Feature] Part__Feature058  label="423001003001001"
  Placement = pos=(68,14.5,68) rot=(1,0,0;1.5708rad)
  shape: bbox 9 x 4 x 9 mm, 22 faces (baked)
FEATURE [Part::Feature] Part__Feature059  label="212002001001"
  Placement = pos=(68,17.5,48) rot=(1,0,0;1.5708rad)
  shape: bbox 7 x 0.5 x 7 mm, 6 faces (baked)
FEATURE [Part::Feature] Part__Feature060  label="212002001001001"
  Placement = pos=(68,17.5,68) rot=(1,0,0;1.5708rad)
  shape: bbox 7 x 0.5 x 7 mm, 6 faces (baked)
FEATURE [Part::Feature] Part__Feature061  label="212002001001002"
  Placement = pos=(55,17.5,58) rot=(1,0,0;1.5708rad)
  shape: bbox 7 x 0.5 x 7 mm, 6 faces (baked)
FEATURE [Part::Box] Box028  label="Cube028"
  AttacherType = Attacher::AttachEngine3D
  Height = 40
  Length = 13
  Placement = pos=(55,12.5,41) rot=(0,0,1;0rad)
  Width = 8.5
FEATURE [Part::Cylinder] Cylinder046  label="Cylinder026"
  Angle = 360
  AttacherType = Attacher::AttachEngine3D
  Height = 10
  Placement = pos=(55,21,58) rot=(1,0,0;1.5708rad)
  Radius = 3
FEATURE [Part::Cylinder] Cylinder047  label="Cylinder027"
  Angle = 360
  AttacherType = Attacher::AttachEngine3D
  Height = 10
  Placement = pos=(55,17.5,58) rot=(1,0,0;1.5708rad)
  Radius = 5.5
FEATURE [Part::Cylinder] Cylinder048  label="Cylinder088"
  Angle = 360
  AttacherType = Attacher::AttachEngine3D
  Height = 10
  Placement = pos=(68,17.5,68) rot=(1,0,0;1.5708rad)
  Radius = 5.5
FEATURE [Part::Cylinder] Cylinder049  label="Cylinder089"
  Angle = 360
  AttacherType = Attacher::AttachEngine3D
  Height = 10
  Placement = pos=(68,21,68) rot=(1,0,0;1.5708rad)
  Radius = 3
FEATURE [Part::Cylinder] Cylinder050  label="Cylinder090"
  Angle = 360
  AttacherType = Attacher::AttachEngine3D
  Height = 10
  Placement = pos=(68,17.5,48) rot=(1,0,0;1.5708rad)
  Radius = 5.5
FEATURE [Part::Cylinder] Cylinder051  label="Cylinder091"
  Angle = 360
  AttacherType = Attacher::AttachEngine3D
  Height = 10
  Placement = pos=(68,21,48) rot=(1,0,0;1.5708rad)
  Radius = 3
FEATURE [Part::Cylinder] Cylinder052  label="Cylinder092"
  Angle = 360
  AttacherType = Attacher::AttachEngine3D
  Height = 30
  Placement = pos=(68,26,48) rot=(1,0,0;1.5708rad)
  Radius = 1.7
FEATURE [Part::Cylinder] Cylinder053  label="Cylinder052"
  Angle = 360
  AttacherType = Attacher::AttachEngine3D
  Height = 30
  Placement = pos=(68,27,68) rot=(1,0,0;1.5708rad)
  Radius = 1.7
FEATURE [Part::Cylinder] Cylinder054  label="Cylinder093"
  Angle = 360
  AttacherType = Attacher::AttachEngine3D
  Height = 30
  Placement = pos=(55,26,58) rot=(1,0,0;1.5708rad)
  Radius = 1.7
FEATURE [Part::MultiFuse] Fusion027  label="trolley-hubs"
  Shapes = -> [Cylinder046,Cylinder049,Cylinder051]
FEATURE [Part::MultiFuse] Fusion028  label="trolley-clearances-and-screws"
  Shapes = -> [Cylinder047,Cylinder048,Cylinder050,Cylinder052,Cylinder053,Cylinder054]
FEATURE [Part::Feature] Part__Feature062  label="212002001001003"
  Placement = pos=(68,13,48) rot=(1,0,0;1.5708rad)
  shape: bbox 7 x 0.5 x 7 mm, 6 faces (baked)
FEATURE [Part::Feature] Part__Feature063  label="212002001001001001"
  Placement = pos=(68,13,68) rot=(1,0,0;1.5708rad)
  shape: bbox 7 x 0.5 x 7 mm, 6 faces (baked)
FEATURE [Part::Feature] Part__Feature064  label="212002001001002001"
  Placement = pos=(55,13,58) rot=(1,0,0;1.5708rad)
  shape: bbox 7 x 0.5 x 7 mm, 6 faces (baked)
FEATURE [Part::MultiFuse] Fusion029
  Shapes = -> [Box028,Fusion027]
FEATURE [Part::Cut] Cut017  label="trolley-blank-a"
  Base = -> Fusion029
  Tool = -> Fusion028
FEATURE [Part::Box] Box029  label="Cube029"
  AttacherType = Attacher::AttachEngine3D
  Height = 40
  Length = 13
  Placement = pos=(55,9.5,41) rot=(0,0,1;0rad)
  Width = 3
FEATURE [Part::Cylinder] Cylinder055  label="Cylinder094"
  Angle = 360
  AttacherType = Attacher::AttachEngine3D
  Height = 3
  Placement = pos=(55,12.5,58) rot=(1,0,0;1.5708rad)
  Radius = 3
FEATURE [Part::Cylinder] Cylinder056  label="Cylinder095"
  Angle = 360
  AttacherType = Attacher::AttachEngine3D
  Height = 3
  Placement = pos=(68,12.5,68) rot=(1,0,0;1.5708rad)
  Radius = 3
FEATURE [Part::Cylinder] Cylinder057  label="Cylinder096"
  Angle = 360
  AttacherType = Attacher::AttachEngine3D
  Height = 3
  Placement = pos=(68,12.5,48) rot=(1,0,0;1.5708rad)
  Radius = 3
FEATURE [Part::Cylinder] Cylinder058  label="Cylinder097"
  Angle = 360
  AttacherType = Attacher::AttachEngine3D
  Height = 30
  Placement = pos=(55,26,58) rot=(1,0,0;1.5708rad)
  Radius = 1.7
FEATURE [Part::Cylinder] Cylinder059  label="Cylinder098"
  Angle = 360
  AttacherType = Attacher::AttachEngine3D
  Height = 30
  Placement = pos=(68,26,48) rot=(1,0,0;1.5708rad)
  Radius = 1.7
FEATURE [Part::Cylinder] Cylinder060  label="Cylinder059"
  Angle = 360
  AttacherType = Attacher::AttachEngine3D
  Height = 30
  Placement = pos=(68,27,68) rot=(1,0,0;1.5708rad)
  Radius = 1.7
FEATURE [Part::MultiFuse] Fusion032
  Shapes = -> [Cylinder058,Cylinder059,Cylinder060]
FEATURE [Part::Box] Box030  label="M3-nut-hole"
  AttacherType = Attacher::AttachEngine3D
  Height = 2.5
  Length = 5.5
  Placement = pos=(59,11.7,74) rot=(0,0,1;0rad)
  Width = 10
FEATURE [Part::Cut] Cut019  label="trolley-a"
  Base = -> Cut017
  Tool = -> Box030
FEATURE [Part::Box] Box031  label="M3-nut-hole001"
  AttacherType = Attacher::AttachEngine3D
  Height = 2.5
  Length = 5.5
  Placement = pos=(59,11.7,74) rot=(0,0,1;0rad)
  Width = 10
FEATURE [Part::Cylinder] Cylinder061  label="wing-clearance001"
  Angle = 360
  AttacherType = Attacher::AttachEngine3D
  Height = 9
  Placement = pos=(25,0,41) rot=(0,0,1;0rad)
  Radius = 4
FEATURE [Part::Box] Box032  label="wings"
  AttacherType = Attacher::AttachEngine3D
  Height = 13
  Length = 18
  Placement = pos=(16,-1.35,41) rot=(0,0,1;0rad)
  Width = 2.7
FEATURE [Part::Cylinder] Cylinder062  label="m3-studding005"
  Angle = 360
  AttacherType = Attacher::AttachEngine3D
  Height = 200
  Placement = pos=(25,0,24) rot=(0,0,1;0rad)
  Radius = 1.5
FEATURE [Part::MultiFuse] Fusion033  label="wing-nut"
  Shapes = -> [Cylinder061,Box032]
FEATURE [Part::MultiFuse] Fusion034
  Shapes = -> [Cylinder062,Fusion033]
FEATURE [Part::Cut] Cut021  label="1311-b"
  Base = -> Fusion
  Tool = -> Fusion034
FEATURE [Part::Feature] Part__Feature065  label="204001001001"
  Placement = pos=(25,0,32.5) rot=(0.995731,-0.092303,0;3.14159rad)
  shape: bbox 6.243 x 5.99 x 4 mm, 28 faces (baked)
FEATURE [Part::Feature] Part__Feature066  label="212001001001"
  Placement = pos=(25,0,38) rot=(0.905883,0.423527,0;3.14159rad)
  shape: bbox 7 x 7 x 0.5 mm, 6 faces (baked)
FEATURE [Part::Box] Box033  label="Cube030"
  AttacherType = Attacher::AttachEngine3D
  Height = 80
  Length = 10
  Placement = pos=(71.5,10,25) rot=(0,0,1;0rad)
  Width = 10
FEATURE [Part::Box] Box034  label="Cube031"
  AttacherType = Attacher::AttachEngine3D
  Height = 122
  Length = 10
  Placement = pos=(62.5,12.75,10) rot=(0,0,1;0rad)
  Width = 4.5
FEATURE [Part::Cut] Cut022
  Base = -> Box033
  Tool = -> Box034
FEATURE [Part::Chamfer] Chamfer
  Base = -> Cut022
  Edges = 2 edges r=0.9: [Edge2,Edge22]
  Placement = pos=(0,0,3) rot=(0,0,1;0rad)
FEATURE [Part::Box] Box035  label="Cube032"
  AttacherType = Attacher::AttachEngine3D
  Height = 7
  Length = 50
  Placement = pos=(31.5,10,26) rot=(0,0,1;0rad)
  Width = 10
FEATURE [Part::Box] Box037  label="Cube034"
  AttacherType = Attacher::AttachEngine3D
  Height = 5
  Length = 60
  Placement = pos=(22,25,65) rot=(0,0,1;0rad)
  Width = 6
FEATURE [Part::Box] Box038  label="Cube035"
  AttacherType = Attacher::AttachEngine3D
  Height = 5
  Length = 8
  Placement = pos=(81.5,10,65) rot=(0,0,1;0rad)
  Width = 21
FEATURE [Part::Feature] Part__Feature067  label="423001003001002"
  Placement = pos=(61.5,15,27) rot=(0,0,1;0.10732rad)
  shape: bbox 9 x 9 x 4 mm, 22 faces (baked)
FEATURE [Part::Box] Box039  label="Cube036"
  AttacherType = Attacher::AttachEngine3D
  Height = 5
  Length = 20
  Placement = pos=(51.5,10,21) rot=(0,0,1;0rad)
  Width = 10
FEATURE [Part::Cylinder] Cylinder063  label="nut-clearance"
  Angle = 360
  AttacherType = Attacher::AttachEngine3D
  Height = 50
  Placement = pos=(61.5,15,2) rot=(0,0,1;0rad)
  Radius = 2.5
FEATURE [Part::Cylinder] Cylinder064  label="bearing-cavity"
  Angle = 360
  AttacherType = Attacher::AttachEngine3D
  Height = 4
  Placement = pos=(61.5,15,25) rot=(0,0,1;0rad)
  Radius = 4.5
FEATURE [Part::Cylinder] Cylinder065  label="m3-studding006"
  Angle = 360
  AttacherType = Attacher::AttachEngine3D
  Height = 50
  Placement = pos=(68.5,15,2) rot=(0,0,1;0rad)
  Radius = 1.7
FEATURE [Part::Cylinder] Cylinder066  label="m3-studding007"
  Angle = 360
  AttacherType = Attacher::AttachEngine3D
  Height = 50
  Placement = pos=(54.5,15,2) rot=(0,0,1;0rad)
  Radius = 1.7
FEATURE [Part::Box] Box040  label="Cube037"
  AttacherType = Attacher::AttachEngine3D
  Height = 7
  Length = 50
  Placement = pos=(31,9.5,26) rot=(0,0,1;0rad)
  Width = 11
FEATURE [Part::Cut] Cut023  label="gearbox-blank-b"
  Base = -> Cut
  Tool = -> Box040
FEATURE [Part::MultiFuse] Fusion035  label="track-blank-a"
  Shapes = -> [Chamfer,Box035]
FEATURE [Part::MultiFuse] Fusion036  label="bearing-nuts"
  Shapes = -> [Cylinder064,Cylinder063]
FEATURE [Part::MultiFuse] Fusion037  label="bearing-nuts001"
  Shapes = -> [Cylinder064,Cylinder063]
FEATURE [Part::Cut] Cut024  label="track-blank-b"
  Base = -> Fusion035
  Tool = -> Fusion036
FEATURE [Part::Cut] Cut025  label="bearing-cover-a"
  Base = -> Box039
  Tool = -> Fusion037
FEATURE [Part::Cylinder] Cylinder067  label="m3-studding008"
  Angle = 360
  AttacherType = Attacher::AttachEngine3D
  Height = 50
  Placement = pos=(54.5,15,2) rot=(0,0,1;0rad)
  Radius = 1.7
FEATURE [Part::Cylinder] Cylinder068  label="m3-studding009"
  Angle = 360
  AttacherType = Attacher::AttachEngine3D
  Height = 50
  Placement = pos=(68.5,15,2) rot=(0,0,1;0rad)
  Radius = 1.7
FEATURE [Part::MultiFuse] Fusion038  label="M3-clearance"
  Shapes = -> [Cylinder066,Cylinder065]
FEATURE [Part::Cut] Cut026  label="bearing-cover-b"
  Base = -> Cut025
  Tool = -> Fusion038
FEATURE [Part::MultiFuse] Fusion039  label="M3-clearance004"
  Shapes = -> [Cylinder067,Cylinder068]
FEATURE [Part::Cut] Cut027  label="track-blank-c"
  Base = -> Cut024
  Tool = -> Fusion039
FEATURE [Part::Cylinder] Cylinder069  label="m3-studding010"
  Angle = 360
  AttacherType = Attacher::AttachEngine3D
  Height = 50
  Placement = pos=(34.5,20,-6) rot=(0,0,1;0rad)
  Radius = 1.7
FEATURE [Part::Cylinder] Cylinder070  label="m3-studding011"
  Angle = 360
  AttacherType = Attacher::AttachEngine3D
  Height = 50
  Placement = pos=(41.5,15,-6) rot=(0,0,1;0rad)
  Radius = 1.7
FEATURE [Part::Box] Box041  label="Cube038"
  AttacherType = Attacher::AttachEngine3D
  Height = 7
  Length = 8
  Placement = pos=(31.5,18,26) rot=(0,0,1;0rad)
  Width = 5
FEATURE [Part::Box] Box042  label="Cube039"
  AttacherType = Attacher::AttachEngine3D
  Height = 7
  Length = 9
  Placement = pos=(31,18.5,26) rot=(0,0,1;0rad)
  Width = 5
FEATURE [Part::MultiFuse] Fusion040  label="track-blank-d"
  Shapes = -> [Box041,Cut027]
FEATURE [Part::Cut] Cut028  label="gearbox-blank-c"
  Base = -> Cut023
  Tool = -> Box042
FEATURE [Part::Cylinder] Cylinder071  label="m3-studding012"
  Angle = 360
  AttacherType = Attacher::AttachEngine3D
  Height = 50
  Placement = pos=(34.5,20,-6) rot=(0,0,1;0rad)
  Radius = 1.4
FEATURE [Part::Cylinder] Cylinder072  label="m3-studding013"
  Angle = 360
  AttacherType = Attacher::AttachEngine3D
  Height = 50
  Placement = pos=(41.5,15,-6) rot=(0,0,1;0rad)
  Radius = 1.4
FEATURE [Part::MultiFuse] Fusion041  label="M3-clearance001"
  Shapes = -> [Cylinder069,Cylinder070]
FEATURE [Part::Cut] Cut029  label="track-blank-e"
  Base = -> Fusion040
  Tool = -> Fusion041
FEATURE [Part::MultiFuse] Fusion042  label="M3-tap001"
  Placement = pos=(0,0,10) rot=(0,0,1;0rad)
  Shapes = -> [Cylinder071,Cylinder072]
FEATURE [Part::Cut] Cut030  label="gearbox-blank-e"
  Base = -> Cut028
  Tool = -> Fusion042
FEATURE [Part::MultiFuse] Fusion043  label="track-clamp-a"
  Shapes = -> [Box037,Box038]
FEATURE [Part::Chamfer] Chamfer005  label="track-clamp-b"
  Base = -> Fusion043
  Edges = 1 edges r=4: [Edge6]
FEATURE [Part::Cylinder] Cylinder073  label="filament008"
  Angle = 360
  AttacherType = Attacher::AttachEngine3D
  Height = 50
  Placement = pos=(31,61,67.5) rot=(1,0,0;1.5708rad)
  Radius = 1.7
FEATURE [Part::Cylinder] Cylinder074  label="filament009"
  Angle = 360
  AttacherType = Attacher::AttachEngine3D
  Height = 50
  Placement = pos=(25,61,67.5) rot=(1,0,0;1.5708rad)
  Radius = 1.7
FEATURE [Part::Cylinder] Cylinder075  label="filament010"
  Angle = 360
  AttacherType = Attacher::AttachEngine3D
  Height = 50
  Placement = pos=(31,61,67.5) rot=(1,0,0;1.5708rad)
  Radius = 1.4
FEATURE [Part::Cylinder] Cylinder076  label="filament011"
  Angle = 360
  AttacherType = Attacher::AttachEngine3D
  Height = 50
  Placement = pos=(25,61,67.5) rot=(1,0,0;1.5708rad)
  Radius = 1.4
FEATURE [Part::MultiFuse] Fusion044  label="M3-clearance002"
  Shapes = -> [Cylinder073,Cylinder074]
FEATURE [Part::MultiFuse] Fusion045  label="M3-tap002"
  Shapes = -> [Cylinder076,Cylinder075]
FEATURE [Part::Cut] Cut031  label="track-clamp-c"
  Base = -> Chamfer005
  Tool = -> Fusion044
FEATURE [Part::Chamfer] Chamfer006  label="trolley-b"
  Base = -> Cut019
  Edges = 6 edges r=2.5: [Edge8,Edge26,Edge46,Edge52,Edge53,Edge64]
FEATURE [Part::Cut] Cut033  label="trolley-b001"
  Base = -> Chamfer006
  Tool = -> Cylinder045
FEATURE [Part::Cylinder] Cylinder077  label="m3-studding014"
  Angle = 360
  AttacherType = Attacher::AttachEngine3D
  Height = 200
  Placement = pos=(14,21,0) rot=(0,0,1;0rad)
  Radius = 1.75
FEATURE [Part::Cylinder] Cylinder078  label="m3-studding015"
  Angle = 360
  AttacherType = Attacher::AttachEngine3D
  Height = 200
  Placement = pos=(24,-22,0) rot=(0,0,1;0rad)
  Radius = 1.75
FEATURE [Part::MultiFuse] Fusion046  label="long-stack-studding-a"
  Shapes = -> [Cylinder031,Cylinder032]
FEATURE [Part::Cut] Cut034  label="gearbox-h"
  Base = -> Cut030
  Tool = -> Fusion046
FEATURE [Part::MultiFuse] Fusion047  label="long-stack-studding-a001"
  Shapes = -> [Cylinder077,Cylinder078]
FEATURE [Part::Cylinder] Cylinder079  label="m3-studding016"
  Angle = 360
  AttacherType = Attacher::AttachEngine3D
  Height = 50
  Placement = pos=(36,0,27) rot=(0,0,1;0rad)
  Radius = 1.7
FEATURE [Part::Cylinder] Cylinder080  label="m3-studding017"
  Angle = 360
  AttacherType = Attacher::AttachEngine3D
  Height = 50
  Placement = pos=(42.5,7,27) rot=(0,0,1;0rad)
  Radius = 1.7
FEATURE [Part::Cylinder] Cylinder081  label="m3-studding018"
  Angle = 360
  AttacherType = Attacher::AttachEngine3D
  Height = 50
  Placement = pos=(42,22,27) rot=(0,0,1;0rad)
  Radius = 1.7
FEATURE [Part::Cylinder] Cylinder082  label="m3-studding019"
  Angle = 360
  AttacherType = Attacher::AttachEngine3D
  Height = 50
  Placement = pos=(41,-9,27) rot=(0,0,1;0rad)
  Radius = 1.7
FEATURE [Part::MultiFuse] Fusion048  label="M3-clearance003"
  Shapes = -> [Cylinder079,Cylinder082,Cylinder081,Cylinder080]
FEATURE [Part::Cylinder] Cylinder083  label="m3-studding020"
  Angle = 360
  AttacherType = Attacher::AttachEngine3D
  Height = 50
  Placement = pos=(36,0,27) rot=(0,0,1;0rad)
  Radius = 1.4
FEATURE [Part::Cylinder] Cylinder084  label="m3-studding021"
  Angle = 360
  AttacherType = Attacher::AttachEngine3D
  Height = 50
  Placement = pos=(41,-9,27) rot=(0,0,1;0rad)
  Radius = 1.4
FEATURE [Part::Cylinder] Cylinder085  label="m3-studding022"
  Angle = 360
  AttacherType = Attacher::AttachEngine3D
  Height = 50
  Placement = pos=(42,22,27) rot=(0,0,1;0rad)
  Radius = 1.4
FEATURE [Part::Cylinder] Cylinder086  label="m3-studding023"
  Angle = 360
  AttacherType = Attacher::AttachEngine3D
  Height = 50
  Placement = pos=(42.5,7,27) rot=(0,0,1;0rad)
  Radius = 1.4
FEATURE [Part::MultiFuse] Fusion049  label="M3-tap003"
  Shapes = -> [Cylinder083,Cylinder084,Cylinder086,Cylinder085]
FEATURE [Part::Cut] Cut036  label="wedge-clamp"
  Base = -> Fusion025
  Placement = pos=(-0.5,0,0) rot=(0,0,1;0rad)
  Tool = -> Fusion049
FEATURE [Part::Cylinder] Cylinder087  label="m3-studding024"
  Angle = 360
  AttacherType = Attacher::AttachEngine3D
  Height = 50
  Placement = pos=(40.5,-9,27) rot=(0,0,1;0rad)
  Radius = 1.75
FEATURE [Part::Cut] Cut038  label="clamp-plate"
  Base = -> Cut016
  Placement = pos=(-0.5,0,0) rot=(0,0,1;0rad)
  Tool = -> Fusion048
FEATURE [Part::MultiFuse] Fusion050  label="trolley-hubs-b"
  Shapes = -> [Cylinder055,Cylinder056,Cylinder057]
FEATURE [Part::MultiFuse] Fusion051  label="trolley-plate-a"
  Shapes = -> [Box029,Fusion050]
FEATURE [Part::Chamfer] Chamfer007
  Base = -> Fusion051
  Edges = 6 edges r=2.5: [Edge6,Edge18,Edge29,Edge31,Edge32,Edge35]
FEATURE [Part::Cut] Cut039  label="trolley-plate-b"
  Base = -> Chamfer007
  Tool = -> Fusion032
FEATURE [Part::Cut] Cut040  label="trolley-plate"
  Base = -> Cut039
  Tool = -> Box031
FEATURE [Part::Box] Box043  label="Cube040"
  AttacherType = Attacher::AttachEngine3D
  Height = 30
  Length = 20
  Placement = pos=(-21,-7,29) rot=(0,0,1;0rad)
  Width = 14
FEATURE [Part::Cut] Cut041  label="gearbox"
  Base = -> Cut034
  Tool = -> Box043
FEATURE [App::DocumentObjectGroup] Group003  label="Drive"
  Group = -> [Group001,Part__Feature027,Cylinder007,Part__Mirroring002,Fusion009,Fusion010,Part__Feature066,Part__Feature065,Cut021,Cut041]
FEATURE [Part::Feature] Part__Feature068  label="1310001"
  Placement = pos=(2,0,0) rot=(0,0,1;0rad)
  shape: bbox 13.32 x 18 x 18 mm, 178 faces (baked)
FEATURE [Part::Box] Box044  label="Cube041"
  AttacherType = Attacher::AttachEngine3D
  Height = 20
  Length = 4
  Placement = pos=(0,-10,-10) rot=(0,0,1;0rad)
  Width = 20
FEATURE [Part::Feature] Part__Feature069  label="1310002"
  Placement = pos=(2,0,0) rot=(0,0,1;0rad)
  shape: bbox 13.32 x 18 x 18 mm, 178 faces (baked)
FEATURE [Part::Cylinder] Cylinder088  label="Cylinder099"
  Angle = 360
  AttacherType = Attacher::AttachEngine3D
  Height = 25
  Placement = pos=(-4,0,0) rot=(0,1,0;1.5708rad)
  Radius = 5
FEATURE [Part::Cylinder] Cylinder089  label="Cylinder100"
  Angle = 360
  AttacherType = Attacher::AttachEngine3D
  Height = 10
  Placement = pos=(-2,0,0) rot=(0,1,0;1.5708rad)
  Radius = 1.7
FEATURE [Part::MultiFuse] Fusion053
  Shapes = -> [Part__Feature069,Cylinder088]
FEATURE [Part::MultiCommon] Common  label="gear-blank"
  Shapes = -> [Fusion053,Box044]
FEATURE [Part::Cut] Cut042  label="shaft-gear-a"
  Base = -> Common
  Placement = pos=(0,0,0) rot=(0,-1,0;1.5708rad)
  Tool = -> Cylinder089
FEATURE [Part::Box] Box045  label="Cube042"
  AttacherType = Attacher::AttachEngine3D
  Height = 10
  Length = 15
  Placement = pos=(-4,-6,1) rot=(0,0,1;0rad)
  Width = 10
FEATURE [Part::Cylinder] Cylinder090  label="Cylinder101"
  Angle = 360
  AttacherType = Attacher::AttachEngine3D
  Height = 25
  Placement = pos=(-4,0,0) rot=(0,1,0;1.5708rad)
  Radius = 5
FEATURE [Part::MultiFuse] Fusion054
  Shapes = -> [Part__Feature068,Cylinder090]
FEATURE [Part::Cylinder] Cylinder091  label="Cylinder102"
  Angle = 360
  AttacherType = Attacher::AttachEngine3D
  Height = 10
  Placement = pos=(-2,0,0) rot=(0,1,0;1.5708rad)
  Radius = 1.8
FEATURE [Part::Cut] Cut001
  Base = -> Cylinder091
  Tool = -> Box045
FEATURE [Part::Fuse] Fusion055
FEATURE [Part::Cylinder] Cylinder092  label="Cylinder103"
  Angle = 360
  AttacherType = Attacher::AttachEngine3D
  Height = 10
  Placement = pos=(5,-4.5,0) rot=(0,1,0;1.5708rad)
  Radius = 0.8
FEATURE [Part::Fuse] Fusion056  label="motor"
  Base = -> Cylinder092
  Placement = pos=(61.5,0,17.5) rot=(0.57735,-0.57735,-0.57735;4.18879rad)
  Tool = -> Fusion055
FEATURE [Part::Box] Box046  label="Cube043"
  AttacherType = Attacher::AttachEngine3D
  Height = 20
  Length = 4
  Placement = pos=(0,-10,-10) rot=(0,0,1;0rad)
  Width = 20
FEATURE [Part::MultiCommon] Common001  label="gear-blank001"
  Shapes = -> [Fusion054,Box046]
FEATURE [Part::Cut] Cut002  label="motor-gear"
  Base = -> Common001
  Placement = pos=(61.5,0,13.5) rot=(0.57735,-0.57735,0.57735;2.0944rad)
  Tool = -> Cut001
FEATURE [Part::Feature] Part__Feature070  label="423001001001"
  Placement = pos=(61.5,15,19.5) rot=(0.884914,0.465754,0;3.14159rad)
  shape: bbox 9 x 9 x 4 mm, 22 faces (baked)
FEATURE [Part::Feature] Part__Feature071  label="212001001001001"
  Placement = pos=(61.5,15,17.5) rot=(0,0,1;3.83772rad)
  shape: bbox 7 x 7 x 0.5 mm, 6 faces (baked)
FEATURE [Part::Cylinder] Cylinder013
  Angle = 360
  AttacherType = Attacher::AttachEngine3D
  Height = 74
  Placement = pos=(61.5,15,79.5) rot=(0.707107,-0.707107,0;3.14159rad)
  Radius = 1.5
FEATURE [Part::Cylinder] Cylinder014
  Angle = 360
  AttacherType = Attacher::AttachEngine3D
  Height = 8
  Placement = pos=(0,0,1) rot=(0,0,1;0rad)
  Radius = 4
FEATURE [Part::Box] Box047  label="Cube044"
  AttacherType = Attacher::AttachEngine3D
  Height = 10
  Length = 10
  Placement = pos=(-12.85,-5,0) rot=(0,0,1;0rad)
  Width = 10
FEATURE [Part::Feature] Box001001
  Placement = pos=(-2.09487,-13.6284,0) rot=(0,0,1;1.0472rad)
  shape: bbox 13.66 x 13.66 x 10 mm, 6 faces (baked)
FEATURE [Part::Feature] Box001002
  Placement = pos=(10.7551,-8.62843,0) rot=(0,0,1;2.0944rad)
  shape: bbox 13.66 x 13.66 x 10 mm, 6 faces (baked)
FEATURE [Part::Feature] Box001003
  Placement = pos=(12.85,5,0) rot=(0,0,1;3.14159rad)
  shape: bbox 10 x 10 x 10 mm, 6 faces (baked)
FEATURE [Part::Feature] Box001004
  Placement = pos=(2.09487,13.6284,0) rot=(0,0,1;4.18879rad)
  shape: bbox 13.66 x 13.66 x 10 mm, 6 faces (baked)
FEATURE [Part::Feature] Box001005
  Placement = pos=(-10.7551,8.62843,0) rot=(0,0,-1;1.0472rad)
  shape: bbox 13.66 x 13.66 x 10 mm, 6 faces (baked)
FEATURE [Part::MultiFuse] Fusion057
  Shapes = -> [Box047,Box001005,Box001001,Box001002,Box001003,Box001004]
FEATURE [Part::Cut] Cut043  label="m3-nut"
  Base = -> Cylinder014
  Placement = pos=(0,0,1) rot=(0,0,1;0rad)
  Tool = -> Fusion057
FEATURE [Part::Feature] Part__Feature072  label="423001001001001"
  Placement = pos=(61.5,15,10.5) rot=(0.884914,0.465754,0;3.14159rad)
  shape: bbox 9 x 9 x 4 mm, 22 faces (baked)
FEATURE [Part::Cylinder] Cylinder015
  Angle = 360
  AttacherType = Attacher::AttachEngine3D
  Height = 100
  Placement = pos=(0,0,-12) rot=(0,0,1;0rad)
  Radius = 1.7
FEATURE [Part::MultiFuse] Fusion052
  Shapes = -> [Cylinder015,Cut043]
FEATURE [Part::Cut] Cut044  label="shaft-gear"
  Base = -> Cut042
  Placement = pos=(61.5,15,17.5) rot=(0.707107,-0.707107,0;3.14159rad)
  Tool = -> Fusion052
FEATURE [Part::Box] Box001006  label="Cube045"
  AttacherType = Attacher::AttachEngine3D
  Height = 10
  Length = 39
  Placement = pos=(-12,-12,0) rot=(0,0,1;0rad)
  Width = 24
FEATURE [Part::Cylinder] Cylinder093  label="Cylinder104"
  Angle = 360
  AttacherType = Attacher::AttachEngine3D
  Height = 30
  Placement = pos=(0,0,-12) rot=(0,0,1;0rad)
  Radius = 3.5
FEATURE [Part::Cylinder] Cylinder094  label="Cylinder105"
  Angle = 360
  AttacherType = Attacher::AttachEngine3D
  Height = 30
  Placement = pos=(0,0,-21.5) rot=(0,0,1;0rad)
  Radius = 4.7
FEATURE [Part::Cylinder] Cylinder095  label="Cylinder106"
  Angle = 360
  AttacherType = Attacher::AttachEngine3D
  Height = 30
  Placement = pos=(0,0,-25.5) rot=(0,0,1;0rad)
  Radius = 10
FEATURE [Part::Cylinder] Cylinder096  label="Cylinder107"
  Angle = 360
  AttacherType = Attacher::AttachEngine3D
  Height = 30
  Placement = pos=(16,0,-25.5) rot=(0,0,1;0rad)
  Radius = 10
FEATURE [Part::Cylinder] Cylinder097  label="Cylinder108"
  Angle = 360
  AttacherType = Attacher::AttachEngine3D
  Height = 30
  Placement = pos=(17,0,-12.5) rot=(0,0,1;0rad)
  Radius = 2.1
FEATURE [Part::Cylinder] Cylinder098  label="Cylinder109"
  Angle = 360
  AttacherType = Attacher::AttachEngine3D
  Height = 30
  Placement = pos=(17,-4.5,-12.5) rot=(0,0,1;0rad)
  Radius = 1
FEATURE [Part::Cylinder] Cylinder099  label="Cylinder110"
  Angle = 360
  AttacherType = Attacher::AttachEngine3D
  Height = 30
  Placement = pos=(17,4.5,-12.5) rot=(0,0,1;0rad)
  Radius = 1
FEATURE [Part::Cylinder] Cylinder023  label="Cylinder111"
  Angle = 360
  AttacherType = Attacher::AttachEngine3D
  Height = 30
  Placement = pos=(13,0,-12.5) rot=(0,0,1;0rad)
  Radius = 2.1
FEATURE [Part::Cylinder] Cylinder100  label="Cylinder112"
  Angle = 360
  AttacherType = Attacher::AttachEngine3D
  Height = 30
  Placement = pos=(13,-4.5,-12.5) rot=(0,0,1;0rad)
  Radius = 1
FEATURE [Part::Cylinder] Cylinder101  label="Cylinder113"
  Angle = 360
  AttacherType = Attacher::AttachEngine3D
  Height = 30
  Placement = pos=(13,4.5,-12.5) rot=(0,0,1;0rad)
  Radius = 1
FEATURE [Part::Box] Box001007  label="Cube046"
  AttacherType = Attacher::AttachEngine3D
  Height = 27
  Length = 4
  Placement = pos=(13,-2.1,-11) rot=(0,0,1;0rad)
  Width = 4.2
FEATURE [Part::Box] Box001008  label="Cube047"
  AttacherType = Attacher::AttachEngine3D
  Height = 27
  Length = 4
  Placement = pos=(13,-5.5,-11) rot=(0,0,1;0rad)
  Width = 2
FEATURE [Part::Box] Box001009  label="Cube048"
  AttacherType = Attacher::AttachEngine3D
  Height = 27
  Length = 4
  Placement = pos=(13,3.5,-11) rot=(0,0,1;0rad)
  Width = 2
FEATURE [Part::MultiFuse] Fusion058  label="motor-slots"
  Shapes = -> [Box001009,Cylinder098,Cylinder099,Box001007,Cylinder097,Cylinder023,Cylinder100,Box001008,Cylinder101]
FEATURE [Part::Cylinder] Cylinder102  label="Cylinder114"
  Angle = 360
  AttacherType = Attacher::AttachEngine3D
  Height = 30
  Placement = pos=(15,0,-25.5) rot=(0,0,1;0rad)
  Radius = 10
FEATURE [Part::MultiFuse] Fusion059  label="gearbox-cavity-1"
  Shapes = -> [Cylinder096,Cylinder093,Cylinder094,Cylinder095,Cylinder102]
FEATURE [Part::MultiFuse] Fusion060  label="gearbox-cavity-2"
  Shapes = -> [Fusion059,Fusion058]
FEATURE [Part::Cut] Cut005  label="gearbox-1"
  Base = -> Box001006
  Tool = -> Fusion060
FEATURE [Part::Chamfer] Chamfer008  label="gearbox-2"
  Base = -> Cut005
  Edges = 10 edges r=1: [Edge47,Edge50,Edge52,Edge54,Edge55,Edge58,Edge60,Edge62,Edge64,Edge65]
FEATURE [Part::Box] Box001010  label="Cube049"
  AttacherType = Attacher::AttachEngine3D
  Height = 8
  Length = 14
  Placement = pos=(-7,-15,-8.5) rot=(0,0,1;0rad)
  Width = 30
FEATURE [Part::Box] Box001011  label="Cube050"
  AttacherType = Attacher::AttachEngine3D
  Height = 11
  Length = 14
  Placement = pos=(-7,-15,-1) rot=(0,0,1;0rad)
  Width = 2.8
FEATURE [Part::Box] Box001012  label="Cube051"
  AttacherType = Attacher::AttachEngine3D
  Height = 11
  Length = 14
  Placement = pos=(-7,12.2,-1) rot=(0,0,1;0rad)
  Width = 2.8
FEATURE [Part::MultiFuse] Fusion061  label="bearing-clamp-1"
  Shapes = -> [Box001010,Box001012,Box001011]
FEATURE [Part::Cylinder] Cylinder027  label="M3-tap-1"
  Angle = 360
  AttacherType = Attacher::AttachEngine3D
  Height = 19
  Placement = pos=(-4,24,6) rot=(1,0,0;1.5708rad)
  Radius = 1.4
FEATURE [Part::Cylinder] Cylinder103  label="M3-tap-2"
  Angle = 360
  AttacherType = Attacher::AttachEngine3D
  Height = 19
  Placement = pos=(4,24,6) rot=(1,0,0;1.5708rad)
  Radius = 1.4
FEATURE [Part::Cylinder] Cylinder104  label="M3-clear-1"
  Angle = 360
  AttacherType = Attacher::AttachEngine3D
  Height = 19
  Placement = pos=(-4,24,6) rot=(1,0,0;1.5708rad)
  Radius = 1.7
FEATURE [Part::Cylinder] Cylinder030  label="M3-clear-2"
  Angle = 360
  AttacherType = Attacher::AttachEngine3D
  Height = 19
  Placement = pos=(4,24,6) rot=(1,0,0;1.5708rad)
  Radius = 1.7
FEATURE [Part::Cylinder] Cylinder105  label="M3-tap-003"
  Angle = 360
  AttacherType = Attacher::AttachEngine3D
  Height = 19
  Placement = pos=(-4,24,6) rot=(1,0,0;1.5708rad)
  Radius = 1.4
FEATURE [Part::Cylinder] Cylinder106  label="M3-tap-004"
  Angle = 360
  AttacherType = Attacher::AttachEngine3D
  Height = 19
  Placement = pos=(4,24,6) rot=(1,0,0;1.5708rad)
  Radius = 1.4
FEATURE [Part::Cylinder] Cylinder107  label="M3-clear-003"
  Angle = 360
  AttacherType = Attacher::AttachEngine3D
  Height = 19
  Placement = pos=(4,24,6) rot=(1,0,0;1.5708rad)
  Radius = 1.7
FEATURE [Part::Cylinder] Cylinder108  label="M3-clear-004"
  Angle = 360
  AttacherType = Attacher::AttachEngine3D
  Height = 19
  Placement = pos=(-4,24,6) rot=(1,0,0;1.5708rad)
  Radius = 1.7
FEATURE [Part::Mirroring] Part__Mirroring011  label="M3-tap-003 (Mirror #1)"
  Base = (0,0,0)
  Normal = (0,1,0)
  Source = -> Cylinder105
FEATURE [Part::Mirroring] Part__Mirroring012  label="M3-tap-004 (Mirror #2)"
  Base = (0,0,0)
  Normal = (0,1,0)
  Source = -> Cylinder106
FEATURE [Part::Mirroring] Part__Mirroring013  label="M3-clear-003 (Mirror #3)"
  Base = (0,0,0)
  Normal = (0,1,0)
  Source = -> Cylinder107
FEATURE [Part::Mirroring] Part__Mirroring014  label="M3-clear-004 (Mirror #4)"
  Base = (0,0,0)
  Normal = (0,1,0)
  Source = -> Cylinder108
FEATURE [Part::MultiFuse] Fusion062  label="M3-tap-a"
  Shapes = -> [Cylinder027,Cylinder103,Part__Mirroring011,Part__Mirroring012]
FEATURE [Part::MultiFuse] Fusion063  label="M3-clear-a"
  Shapes = -> [Cylinder104,Cylinder030,Part__Mirroring013,Part__Mirroring014]
FEATURE [Part::Cut] Cut006  label="bearing-clamp-2"
  Base = -> Fusion061
  Placement = pos=(61.5,14.5,17.5) rot=(0.707107,-0.707107,0;3.14159rad)
  Tool = -> Fusion063
FEATURE [Part::Cut] Cut045  label="gearbox-3"
  Base = -> Chamfer008
  Tool = -> Fusion062
FEATURE [Part::Cylinder] Cylinder109  label="Cylinder115"
  Angle = 360
  AttacherType = Attacher::AttachEngine3D
  Height = 30
  Placement = pos=(0,0,-4.5) rot=(0,0,1;0rad)
  Radius = 4.7
FEATURE [Part::Cylinder] Cylinder110  label="Cylinder116"
  Angle = 360
  AttacherType = Attacher::AttachEngine3D
  Height = 30
  Placement = pos=(0,0,-9) rot=(0,0,1;0rad)
  Radius = 3.5
FEATURE [Part::MultiFuse] Fusion080  label="bearing-nut"
  Placement = pos=(61.5,14.5,17.5) rot=(0.707107,-0.707107,0;3.14159rad)
  Shapes = -> [Cylinder109,Cylinder110]
FEATURE [Part::Chamfer] Chamfer014  label="gearbox-004"
  Base = -> Cut045
  Edges = 5 edges r=0.5: [Edge16,Edge17,Edge18,Edge19,Edge20]
FEATURE [Part::Box] Box001027045199  label="Cube245"
  AttacherType = Attacher::AttachEngine3D
  Height = 8
  Length = 3
  Width = 8
FEATURE [Part::Cylinder] Cylinder267  label="Cylinder285"
  Angle = 360
  AttacherType = Attacher::AttachEngine3D
  Height = 10
  Placement = pos=(-3,4,4.5) rot=(0,1,0;1.5708rad)
  Radius = 2
FEATURE [Part::Fillet] Fillet045
  Base = -> Box001027045199
  Edges = 2 edges r=3: [Edge10,Edge12]
FEATURE [Part::Cut] Cut239  label="cable-tie-holder-1"
  Base = -> Fillet045
  Placement = pos=(25,-4,10) rot=(0,1,0;1.5708rad)
  Tool = -> Cylinder267
FEATURE [Part::MultiFuse] Fusion112154  label="gearbox001"
  Placement = pos=(61.5,15,17.5) rot=(0.707107,-0.707107,0;3.14159rad)
  Shapes = -> [Chamfer014,Cut239]
FEATURE [Part::Cylinder] Cylinder268  label="m3-studding025"
  Angle = 360
  AttacherType = Attacher::AttachEngine3D
  Height = 50
  Placement = pos=(54.5,15,2) rot=(0,0,1;0rad)
  Radius = 1.4
FEATURE [Part::Cylinder] Cylinder269  label="m3-studding026"
  Angle = 360
  AttacherType = Attacher::AttachEngine3D
  Height = 50
  Placement = pos=(68.5,15,2) rot=(0,0,1;0rad)
  Radius = 1.4
FEATURE [Part::MultiFuse] Fusion112155  label="M3-tap-5"
  Shapes = -> [Cylinder268,Cylinder269]
FEATURE [Part::Cut] Cut240  label="bearing-clamp-5"
  Base = -> Cut006
  Tool = -> Fusion112155
FEATURE [Part::Cut] Cut241  label="bearing-clamp-3"
  Base = -> Cut240
  Tool = -> Fusion080
FEATURE [Part::Cylinder] Cylinder270  label="Cylinder286"
  Angle = 360
  AttacherType = Attacher::AttachEngine3D
  Height = 30
  Placement = pos=(57,5,58) rot=(0,1,0;1.5708rad)
  Radius = 1.7
FEATURE [Part::Box] Box001027045200  label="Cube246"
  AttacherType = Attacher::AttachEngine3D
  Height = 10
  Length = 10
  Placement = pos=(71,1,53) rot=(0,0,1;0rad)
  Width = 9
FEATURE [Part::Chamfer] Chamfer015
  Base = -> Box001027045200
  Edges = 1 edges r=2: [Edge3]
  Placement = pos=(-1.5,0,0) rot=(0,0,1;0rad)
FEATURE [Part::Chamfer] Chamfer016
  Base = -> Chamfer015
  Edges = 2 edges r=2: [Edge1,Edge4]
FEATURE [Part::Cylinder] Cylinder271  label="Cylinder287"
  Angle = 360
  AttacherType = Attacher::AttachEngine3D
  Height = 30
  Placement = pos=(74,5,58) rot=(0,1,0;1.5708rad)
  Radius = 2.2
FEATURE [Part::Cut] Cut242
  Base = -> Chamfer016
  Tool = -> Cylinder270
FEATURE [Part::Cut] Cut243
  Base = -> Cut242
  Tool = -> Cylinder271
FEATURE [Part::Fillet] Fillet046
  Base = -> Cut243
  Edges = 2 edges r=3: [Edge2,Edge3]
FEATURE [Part::Cylinder] Cylinder272  label="Cylinder288"
  Angle = 360
  AttacherType = Attacher::AttachEngine3D
  Height = 30
  Placement = pos=(79.5,5,48) rot=(0,1,0;0rad)
  Radius = 2.2
FEATURE [Part::Cut] Cut244  label="led-pt-holder"
  Base = -> Fillet046
  Tool = -> Cylinder272
FEATURE [Part::Cut] Cut245  label="led-pt-holder001"
  Base = -> Fillet046
  Tool = -> Cylinder272
FEATURE [Part::Mirroring] Part__Mirroring015  label="led-pt-holder001 (Mirror #16)"
  Base = (60,0,0)
  Normal = (1,0,0)
  Placement = pos=(18.6,0,0) rot=(0,0,1;0rad)
  Source = -> Cut245
FEATURE [Part::Box] Box001027045201  label="Cube247"
  AttacherType = Attacher::AttachEngine3D
  Height = 8
  Length = 3
  Width = 8
FEATURE [Part::Cylinder] Cylinder273  label="Cylinder289"
  Angle = 360
  AttacherType = Attacher::AttachEngine3D
  Height = 10
  Placement = pos=(-3,4,4.5) rot=(0,1,0;1.5708rad)
  Radius = 2
FEATURE [Part::Fillet] Fillet047
  Base = -> Box001027045201
  Edges = 2 edges r=3: [Edge10,Edge12]
FEATURE [Part::Cut] Cut246  label="cable-tie-holder"
  Base = -> Fillet047
  Placement = pos=(81,11,27) rot=(0.57735,-0.57735,0.57735;2.0944rad)
  Tool = -> Cylinder273
FEATURE [Part::Cut] Cut247  label="cable-tie-holder001"
  Base = -> Fillet047
  Placement = pos=(64,20,49) rot=(0.57735,-0.57735,-0.57735;4.18879rad)
  Tool = -> Cylinder273
FEATURE [Part::Box] Box001027045202  label="Cube248"
  AttacherType = Attacher::AttachEngine3D
  Height = 7
  Length = 68
  Placement = pos=(9,10,101) rot=(0,0,1;0rad)
  Width = 10
FEATURE [Part::Box] Box001027045203  label="Cube249"
  AttacherType = Attacher::AttachEngine3D
  Height = 19
  Length = 10
  Placement = pos=(9,10,89) rot=(0,0,1;0rad)
  Width = 15
FEATURE [Part::Mirroring] Part__Mirroring016  label="led-pt-holder (Mirror #17)"
  Base = (0,0,0)
  Normal = (0,1,0)
  Placement = pos=(0,30,0) rot=(0,0,1;0rad)
  Source = -> Cut244
FEATURE [Part::Mirroring] Part__Mirroring017  label="led-pt-holder (Mirror #17)001"
  Base = (0,0,0)
  Normal = (0,1,0)
  Placement = pos=(0,30,19) rot=(0,0,1;0rad)
  Source = -> Cut244
FEATURE [Part::Mirroring] Part__Mirroring018  label="led-pt-holder (Mirror #17)002"
  Base = (0,0,0)
  Normal = (0,1,0)
  Placement = pos=(0,30,-7) rot=(0,0,1;0rad)
  Source = -> Cut244
FEATURE [Part::MultiFuse] Fusion112158  label="led-holders-1"
  Placement = pos=(0,4,0) rot=(0,0,1;0rad)
  Shapes = -> [Part__Mirroring016,Part__Mirroring018,Part__Mirroring017]
FEATURE [Part::Mirroring] Part__Mirroring019  label="led-pt-holder001 (Mirror #20)"
  Base = (0,0,0)
  Normal = (0,1,0)
  Placement = pos=(0,34,0) rot=(0,0,1;0rad)
  Source = -> Part__Mirroring015
FEATURE [Part::MultiFuse] Fusion112159  label="trolley-d"
  Shapes = -> [Cut247,Cut033]
FEATURE [Part::Cylinder] Cylinder274  label="M3-head"
  Angle = 360
  AttacherType = Attacher::AttachEngine3D
  Height = 3
  Placement = pos=(68,24,68) rot=(1,0,0;1.5708rad)
  Radius = 2.75
FEATURE [App::DocumentObjectGroup] Group002  label="construction"
  Group = -> [Box013,Box014,Box012,Box004,Box005,Box006,Part__Mirroring004,Part__Mirroring005,Part__Mirroring006,Part__Mirroring007,Part__Mirroring009,Part__Mirroring010,Cylinder034,Cut019,Cylinder274,Part__Feature067]
FEATURE [Part::Box] Box001027045204  label="Cube250"
  AttacherType = Attacher::AttachEngine3D
  Height = 17
  Length = 8
  Placement = pos=(71.5,19,46) rot=(0,0,1;0rad)
  Width = 6
FEATURE [Part::Box] Box001027045205  label="Cube251"
  AttacherType = Attacher::AttachEngine3D
  Height = 10
  Length = 8
  Placement = pos=(71.5,19,72) rot=(0,0,1;0rad)
  Width = 6
FEATURE [Part::Box] Box001027045206  label="Cube252"
  AttacherType = Attacher::AttachEngine3D
  Height = 10
  Length = 8
  Placement = pos=(59.1,20,53) rot=(0,0,1;0rad)
  Width = 6
FEATURE [Part::MultiFuse] Fusion112160  label="led-holders"
  Shapes = -> [Fusion112158,Box001027045204,Box001027045205]
FEATURE [Part::MultiFuse] Fusion112161  label="pt-holder"
  Shapes = -> [Part__Mirroring019,Box001027045206]
FEATURE [Part::Mirroring] Part__Mirroring020  label="cable-tie-holder (Mirror #21)"
  Base = (0,0,0)
  Normal = (0,1,0)
  Placement = pos=(0,31,11) rot=(0,0,1;0rad)
  Source = -> Cut246
FEATURE [Part::Chamfer] Chamfer017  label="track-blank-f"
  Base = -> Cut029
  Edges = 2 edges r=2: [Edge35,Edge37]
FEATURE [Part::Box] Box001027045196  label="Cube242"
  AttacherType = Attacher::AttachEngine3D
  Height = 25.5
  Length = 4
  Placement = pos=(70,-2,-49) rot=(0,0,1;0rad)
  Width = 14
FEATURE [Part::Box] Box001027045197  label="Cube243"
  AttacherType = Attacher::AttachEngine3D
  Height = 21.5
  Length = 10
  Placement = pos=(70,7,-47) rot=(0,0,1;0rad)
  Width = 3
FEATURE [Part::Box] Box001027045198  label="Cube244"
  AttacherType = Attacher::AttachEngine3D
  Height = 20.5
  Length = 10
  Placement = pos=(63,7.25,-46.5) rot=(0,0,1;0rad)
  Width = 2.5
FEATURE [Part::MultiFuse] Fusion112152  label="pin-strip-hole"
  Placement = pos=(2,0,0) rot=(0,0,1;0rad)
  Shapes = -> [Box001027045197,Box001027045198]
FEATURE [Part::Cut] Cut238  label="pin-strip-bracket"
  Base = -> Box001027045196
  Placement = pos=(96,21.7,101) rot=(0,1,0;1.5708rad)
  Tool = -> Fusion112152
FEATURE [Part::Cylinder] Cylinder275  label="m3-studding027"
  Angle = 360
  AttacherType = Attacher::AttachEngine3D
  Height = 200
  Placement = pos=(14,21,0) rot=(0,0,1;0rad)
  Radius = 1.75
FEATURE [Part::MultiFuse] Fusion112162  label="end-pillar-1"
  Shapes = -> [Box001027045202,Box001027045203]
FEATURE [Part::Cut] Cut251  label="end-pillar-2"
  Base = -> Fusion112162
  Tool = -> Cylinder275
FEATURE [Part::MultiFuse] Fusion112163  label="roller-track"
  Shapes = -> [Cut251,Cut238,Chamfer017,Part__Mirroring020,Fusion112160]
FEATURE [App::DocumentObjectGroup] Group006  label="Track"
  Group = -> [Cut026,Cut031,Fusion112163]
FEATURE [Part::MultiFuse] Fusion112164  label="trolley"
  Shapes = -> [Fusion112159,Fusion112161]
FEATURE [App::DocumentObjectGroup] Group005  label="Trolley"
  Group = -> [Part__Feature057,Part__Feature058,Part__Feature059,Part__Feature060,Part__Feature061,Part__Feature062,Part__Feature063,Part__Feature064,Part__Feature056,Cut040,Fusion112164]
FEATURE [Part::Cylinder] Cylinder276  label="Cylinder290"
  Angle = 360
  AttacherType = Attacher::AttachEngine3D
  Height = 30
  Placement = pos=(61.5,15,-11) rot=(0,0,1;0rad)
  Radius = 10
FEATURE [Part::Cut] Cut252  label="bearing-clamp"
  Base = -> Cut241
  Tool = -> Cylinder276
FEATURE [App::DocumentObjectGroup] Group007  label="Selector"
  Group = -> [Cut002,Fusion056,Part__Feature070,Part__Feature071,Cylinder013,Part__Feature072,Cut044,Fusion112154,Cut252]
FEATURE [Part::Box] Box001027045207  label="Cube253"
  AttacherType = Attacher::AttachEngine3D
  Height = 4.5
  Length = 10
  Placement = pos=(36,-25,55.85) rot=(0,0,1;0rad)
  Width = 23
FEATURE [Part::Chamfer] Chamfer018
  Base = -> Box001027045207
  Edges = 1 edges r=6: [Edge3]
FEATURE [Part::Box] Box001027045208  label="Cube254"
  AttacherType = Attacher::AttachEngine3D
  Height = 31
  Length = 10
  Placement = pos=(34,-27,47) rot=(0,0,1;0rad)
  Width = 21
FEATURE [Part::Cut] Cut253
  Base = -> Cut004
  Tool = -> Box001027045208
FEATURE [Part::Fillet] Fillet048
  Base = -> Cut253
  Edges = 1 edges r=2: [Edge21]
FEATURE [Part::Box] Box001027045209  label="Cube255"
  AttacherType = Attacher::AttachEngine3D
  Height = 19
  Length = 19
  Placement = pos=(27,-27,51) rot=(0,0,1;0rad)
  Width = 10
FEATURE [Part::Box] Box001027045210  label="Cube256"
  AttacherType = Attacher::AttachEngine3D
  Height = 31
  Length = 2
  Placement = pos=(34,-25,47) rot=(0,0,1;0rad)
  Width = 21
FEATURE [Part::Cylinder] Cylinder277  label="Cylinder291"
  Angle = 360
  AttacherType = Attacher::AttachEngine3D
  Height = 40
  Placement = pos=(35,-20,63) rot=(0,1,0;1.5708rad)
  Radius = 1.7
FEATURE [Part::Cut] Cut254
  Base = -> Box001027045209
  Tool = -> Box001027045210
FEATURE [Part::Chamfer] Chamfer019
  Base = -> Cut254
  Edges = 1 edges r=3: [Edge1]
FEATURE [Part::MultiFuse] Fusion112165
  Shapes = -> [Chamfer018,Chamfer019]
FEATURE [Part::MultiFuse] Fusion112166  label="drive-block-1"
  Shapes = -> [Fillet048,Fusion112165]
FEATURE [Part::Cylinder] Cylinder278  label="Cylinder292"
  Angle = 360
  AttacherType = Attacher::AttachEngine3D
  Height = 40
  Placement = pos=(18,-20,63) rot=(0,1,0;1.5708rad)
  Radius = 1.4
FEATURE [Part::MultiFuse] Fusion112167  label="adjuster-screw"
  Shapes = -> [Cylinder277,Cylinder278]
FEATURE [Part::MultiFuse] Fusion112168  label="holes-1"
  Shapes = -> [Fusion019,Fusion017,Fusion112167,Fusion047,Fusion045,Cylinder087]
FEATURE [Part::Cut] Cut255
  Base = -> Fusion112166
  Tool = -> Fusion112168
FEATURE [Part::MultiFuse] Fusion112169  label="drive-block"
  Shapes = -> [Cut255,Part__Feature055]
FEATURE [Part::MultiFuse] Fusion112170  label="drive-block001"
  Placement = pos=(0,0,19) rot=(0,0,1;0rad)
  Shapes = -> [Cut255,Part__Feature055]
FEATURE [App::DocumentObjectGroup] Group004  label="Filament-Clamp"
  Group = -> [Part__Mirroring003,Part__Mirroring008,Cylinder022,Part__Feature049,Part__Feature050,Part__Feature051,Part__Feature052,Cylinder033,Cylinder026,Cut036,Cut038,Fusion112169,Fusion112170]
